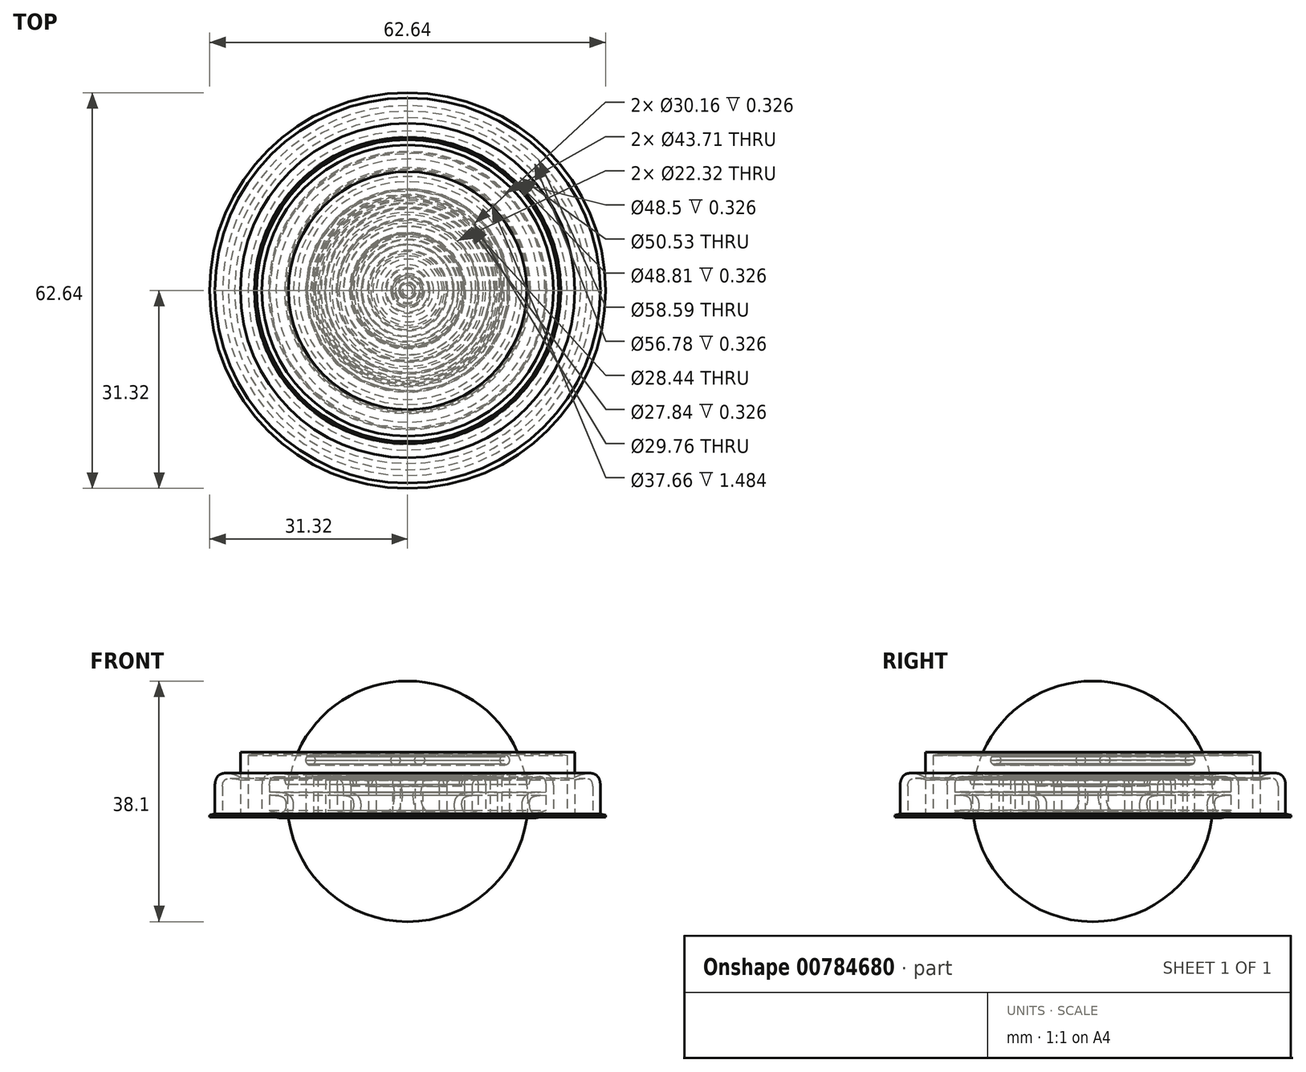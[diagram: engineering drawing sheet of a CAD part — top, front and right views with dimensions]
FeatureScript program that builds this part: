
annotation { "Feature Type Name" : "Feature", "Feature Type Description" : "" }
export const myFeature = defineFeature(function(context is Context, id is Id, definition is map)
    precondition{}
    {
        {
            var Q0;
            Q0=qCreatedBy(makeId("Front.planeOp"),FACE);
            var sketch = newSketch(context, id + "F0", { "sketchPlane" : qUnion([Q0])});
            skLineSegment(sketch, "E0", {"start": v(0, 0) * mm, "end": v(0, 38.1) * mm});
            skArc(sketch, "E1", {"start": v(0, 38.1) * mm, "mid": v(-19.05, 19.05) * mm, "end": v(0, 0) * mm});
            skText(sketch, "E2", { "text": "micaiah\n", "fontName": "Tinos-Regular.ttf"});
            const initialGuessF0  = {"E2": [-0.01539, 0.01655, 1, 0, 0.01067]};
            skSetInitialGuess(sketch, initialGuessF0);
            skSolve(sketch);
        }
        {
            var Q0;
            Q0 = qSketchRegion(id + "F0", true);
            var Q1;
            Q1=sQuery(id+"F0.wireOp",EDGE,"E0");
            revolve(context, id + "F1", {"surfaceOperationType" : NewSurfaceOperationType.NEW, "entities" : qUnion([Q0]), "axis" : qUnion([Q1]), "revolveType" : RevolveType.FULL});
        }
    });
